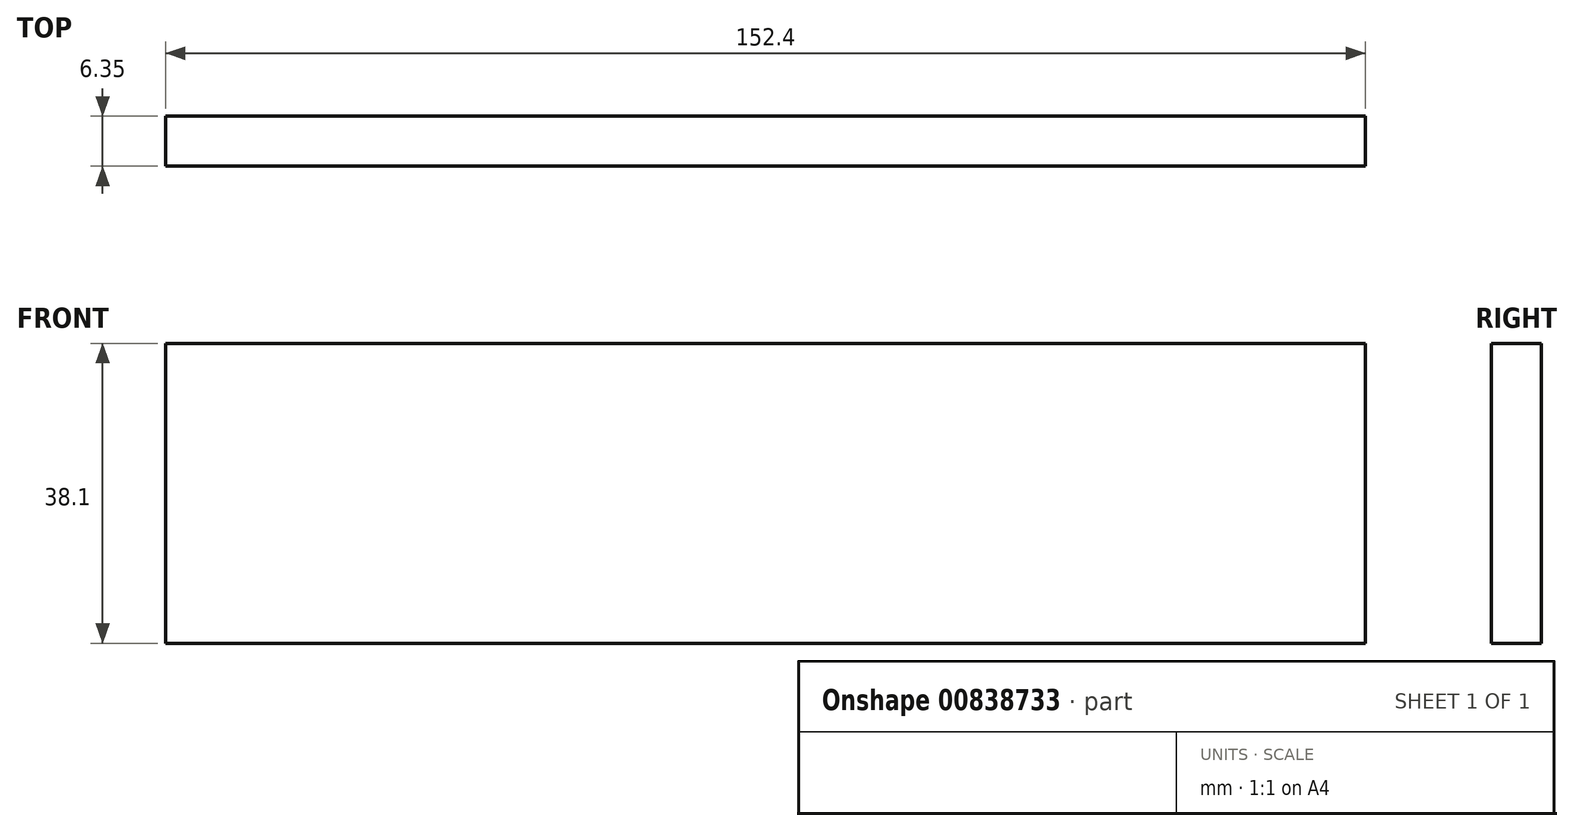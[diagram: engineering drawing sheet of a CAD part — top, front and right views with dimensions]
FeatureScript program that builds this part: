
annotation { "Feature Type Name" : "Feature", "Feature Type Description" : "" }
export const myFeature = defineFeature(function(context is Context, id is Id, definition is map)
    precondition{}
    {
        {
            var Q0;
            Q0=qCreatedBy(makeId("Top.planeOp"),FACE);
            var sketch = newSketch(context, id + "F0", { "sketchPlane" : qUnion([Q0])});
            skLineSegment(sketch, "E0.bottom", {"start": v(0, 0) * mm, "end": v(152.4, 0) * mm});
            skLineSegment(sketch, "E0.top", {"start": v(0, 6.35) * mm, "end": v(152.4, 6.35) * mm});
            skLineSegment(sketch, "E0.left", {"start": v(0, 0) * mm, "end": v(0, 6.35) * mm});
            skLineSegment(sketch, "E0.right", {"start": v(152.4, 0) * mm, "end": v(152.4, 6.35) * mm});
            skSolve(sketch);
        }
        {
            var Q0;
            Q0 = qSketchRegion(id + "F0", true);
            extrude(context, id + "F1", {"entities" : qUnion([Q0]), "depth" : 38.1 * mm, "offsetDistance" : 25.4 * mm});
        }
    });
